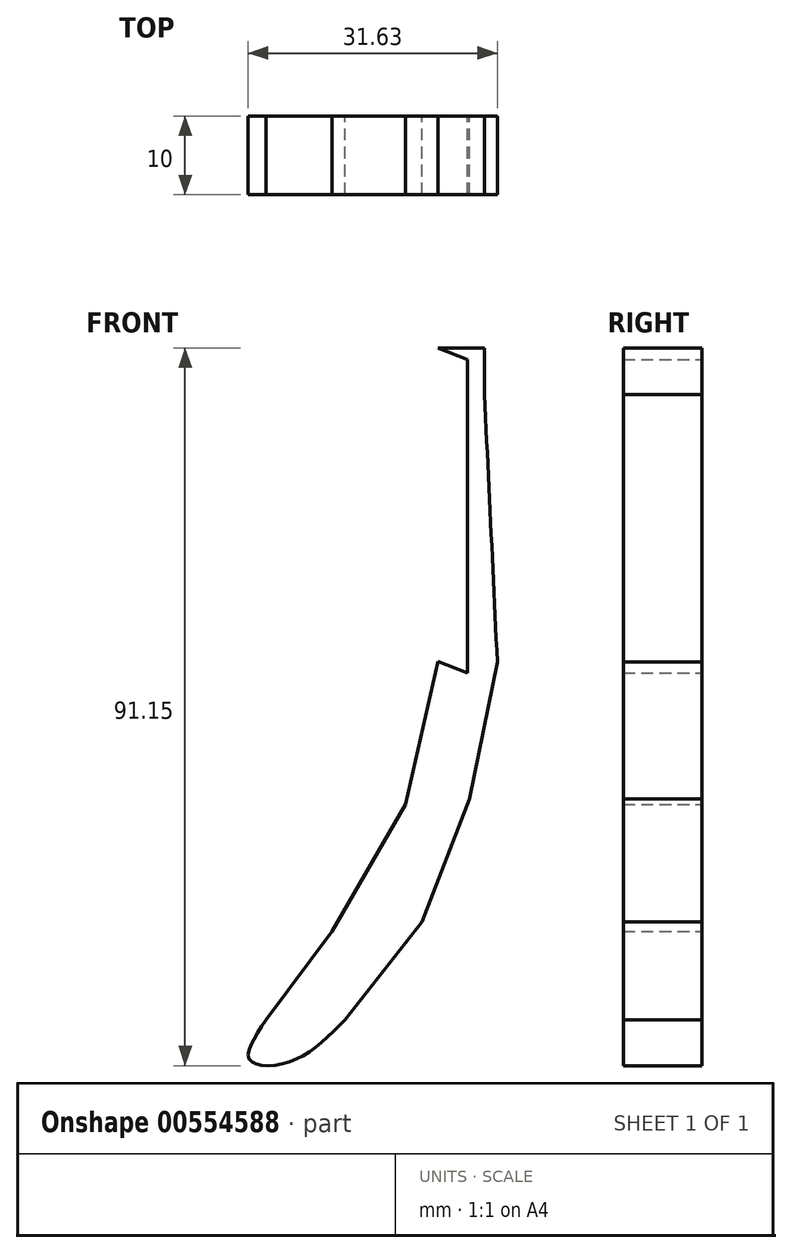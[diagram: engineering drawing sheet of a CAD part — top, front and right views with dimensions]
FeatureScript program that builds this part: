
annotation { "Feature Type Name" : "Feature", "Feature Type Description" : "" }
export const myFeature = defineFeature(function(context is Context, id is Id, definition is map)
    precondition{}
    {
        {
            var Q0;
            Q0=qCreatedBy(makeId("Front.planeOp"),FACE);
            var sketch = newSketch(context, id + "F0", { "sketchPlane" : qUnion([Q0])});
            skLineSegment(sketch, "E0.bottom", {"start": v(-48.75, 44.13) * mm, "end": v(-42.85, 44.13) * mm});
            skLineSegment(sketch, "E0.top", {"start": v(-48.75, 38.23) * mm, "end": v(-42.85, 38.23) * mm});
            skLineSegment(sketch, "E0.left", {"start": v(-48.75, 44.13) * mm, "end": v(-48.75, 38.23) * mm});
            skLineSegment(sketch, "E0.right", {"start": v(-42.85, 44.13) * mm, "end": v(-42.85, 38.23) * mm});
            skFitSpline(sketch, "E1", {"points": [v(-48.75, 38.23) * mm, v(-48.75, 26.06) * mm], "startDerivative": vector(0, -12.17) * mm, "endDerivative": vector(0, -12.17) * mm});
            skFitSpline(sketch, "E2", {"points": [v(-48.75, 26.06) * mm, v(-48.75, 4.34) * mm], "startDerivative": vector(0, -21.72) * mm, "endDerivative": vector(0, -21.72) * mm});
            skFitSpline(sketch, "E3", {"points": [v(-48.75, 4.34) * mm, v(-52.9, -13.83) * mm], "startDerivative": vector(-4.14, -18.16) * mm, "endDerivative": vector(-4.14, -18.16) * mm});
            skFitSpline(sketch, "E4", {"points": [v(-52.9, -13.83) * mm, v(-62.23, -29.97) * mm], "startDerivative": vector(-9.33, -16.15) * mm, "endDerivative": vector(-9.33, -16.15) * mm});
            skFitSpline(sketch, "E5", {"points": [v(-62.23, -29.97) * mm, v(-70.58, -41.22) * mm], "startDerivative": vector(-8.36, -11.25) * mm, "endDerivative": vector(-8.36, -11.25) * mm});
            skFitSpline(sketch, "E6", {"points": [v(-70.58, -41.22) * mm, v(-72.72, -46.21) * mm, v(-67.73, -46.57) * mm, v(-60.6, -41.22) * mm], "startDerivative": vector(-13.28, -19.37) * mm, "endDerivative": vector(16.65, 16.88) * mm});
            skFitSpline(sketch, "E7", {"points": [v(-60.6, -41.22) * mm, v(-50.83, -28.78) * mm], "startDerivative": vector(9.77, 12.44) * mm, "endDerivative": vector(9.77, 12.44) * mm});
            skFitSpline(sketch, "E8", {"points": [v(-50.83, -28.78) * mm, v(-44.77, -13.14) * mm], "startDerivative": vector(6.05, 15.64) * mm, "endDerivative": vector(6.05, 15.64) * mm});
            skFitSpline(sketch, "E9", {"points": [v(-44.77, -13.14) * mm, v(-41.24, 4.27) * mm], "startDerivative": vector(3.53, 17.4) * mm, "endDerivative": vector(3.53, 17.4) * mm});
            skFitSpline(sketch, "E10", {"points": [v(-41.24, 4.27) * mm, v(-42.85, 38.23) * mm], "startDerivative": vector(-1.5, 33.96) * mm, "endDerivative": vector(-1.5, 33.96) * mm});
            skSolve(sketch);
        }
        {
            var Q0;
            Q0 = qSketchRegion(id + "F0", true);
            extrude(context, id + "F1", {"entities" : qUnion([Q0]), "depth" : 10 * mm, "offsetDistance" : 25 * mm});
        }
        {
            var Q0;
            Q0=makeQuery(id+"F1.opExtrude","SWEPT_FACE",FACE,{"disambiguationData":[OSD([sQuery(id+"F0.wireOp",EDGE,"E9")])]});
            var sketch = newSketch(context, id + "F2", { "sketchPlane" : qUnion([Q0])});
            skSolve(sketch);
        }
        {
            var Q0;
            Q0=makeQuery(id+"F1.opExtrude","SWEPT_FACE",FACE,{"disambiguationData":[OSD([sQuery(id+"F0.wireOp",EDGE,"E8")])]});
            var Q1;
            Q1=makeQuery(id+"F1.opExtrude","SWEPT_FACE",FACE,{"disambiguationData":[OSD([sQuery(id+"F0.wireOp",EDGE,"E7")])]});
            var Q2;
            {var subQ0=sQuery(id+"F0.wireOp",EDGE,"E9");Q2=makeQuery(id+"F2.imprint","IMPRINT",FACE,{"disambiguationData":[TD([[makeQuery(id+"F2.imprint","IMPRINT",EDGE,{"derivedFrom":makeQuery(id+"F1.opExtrude","CAP_EDGE",EDGE,{"disambiguationData":[OSD([subQ0])],"isStart":true})}),1.0]])]});}
            var Q3;
            Q3=makeQuery(id+"F1.opExtrude","SWEPT_FACE",FACE,{"disambiguationData":[OSD([sQuery(id+"F0.wireOp",EDGE,"E2")])]});
            var Q4;
            Q4=makeQuery(id+"F1.opExtrude","SWEPT_FACE",FACE,{"disambiguationData":[OSD([sQuery(id+"F0.wireOp",EDGE,"E1")])]});
            extrude(context, id + "F3", {"entities" : qUnion([Q0, Q1, Q2, Q3, Q4]), "operationType" : NewBodyOperationType.REMOVE, "depth" : 4 * mm, "offsetDistance" : 25 * mm});
        }
    });
